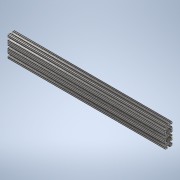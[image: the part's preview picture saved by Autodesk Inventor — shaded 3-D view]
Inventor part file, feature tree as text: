
AUTODESK INVENTOR PART (.ipt)
format: ipt  version: 2020 (Build 240168000, 168)  size: 384,512 bytes
history: native  units: in
note: dims shown in document units (in); Inventor stores cm internally (conversion verified against a paired STEP export)
features: sketch x2, extrude x1
ambient origin geometry x8: Origin, YZ Plane, XZ Plane, XY Plane, X Axis, Y Axis, Z Axis, Center Point
bodies: Solid1 (feature_tree)
feature tree (3):
  extrude  "Extrusion1"  [1 undecoded]
  sketch  "Sketch2"
  sketch  "Sketch1"  dims[d0=22.0in d1=0.0in]
note: 1 required parameter value undecoded (feature->parameter linkage not recoverable at this tier; creation-order binding heuristic only, values carry confidence <= 0.55)
